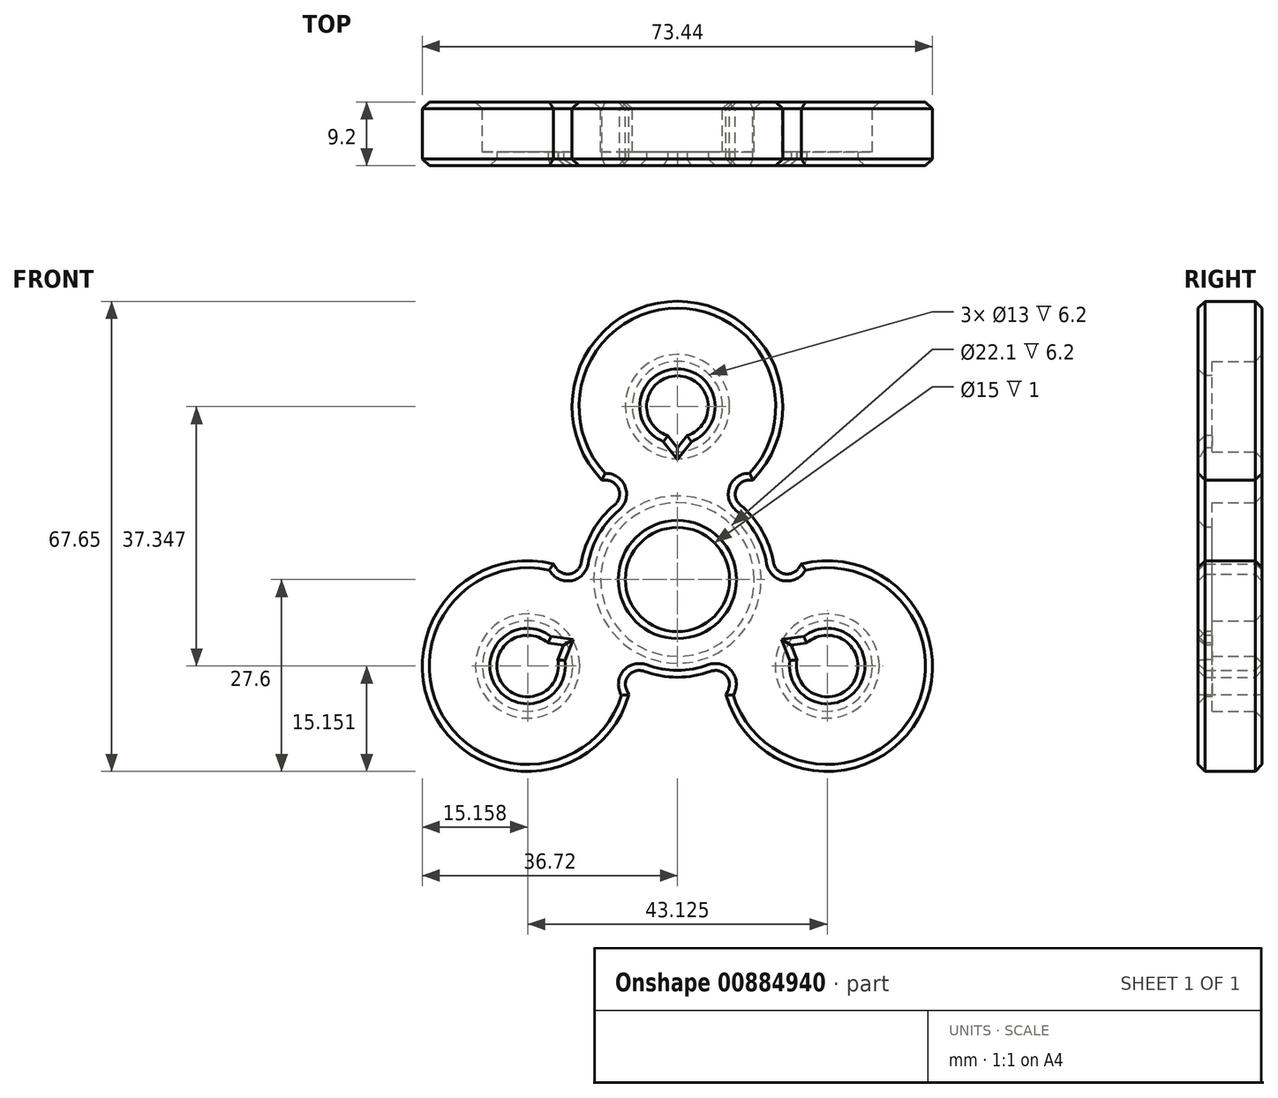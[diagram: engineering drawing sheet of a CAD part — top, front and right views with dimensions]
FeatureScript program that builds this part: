
annotation { "Feature Type Name" : "Feature", "Feature Type Description" : "" }
export const myFeature = defineFeature(function(context is Context, id is Id, definition is map)
    precondition{}
    {
        {
            var Q0;
            Q0=qCreatedBy(makeId("Front.planeOp"),FACE);
            var sketch = newSketch(context, id + "F0", { "sketchPlane" : qUnion([Q0])});
            skCircle(sketch, "E0", {"center": v(0, 0) * mm, "radius": 11.05 * mm});
            skArc(sketch, "E1", {"start": v(-2.48, 13.83) * mm, "mid": v(-12.17, 7.02) * mm, "end": v(-13.22, -4.76) * mm});
            skArc(sketch, "E2.MirrorC", {"start": v(-10.86, 14.33) * mm, "mid": v(0, 40.05) * mm, "end": v(10.86, 14.33) * mm});
            skArc(sketch, "E3.1.0", {"start": v(-6.98, -16.57) * mm, "mid": v(-34.69, -20.03) * mm, "end": v(-17.84, 2.24) * mm});
            skArc(sketch, "E3.2.0", {"start": v(17.84, 2.24) * mm, "mid": v(34.69, -20.03) * mm, "end": v(6.98, -16.57) * mm});
            skLineSegment(sketch, "E4", {"start": v(-10.86, 14.33) * mm, "end": v(-2.48, 13.83) * mm});
            skLineSegment(sketch, "E5.MirrorCS", {"start": v(10.86, 14.33) * mm, "end": v(2.48, 13.83) * mm});
            skLineSegment(sketch, "E6.1.0", {"start": v(-6.98, -16.57) * mm, "end": v(-10.73, -9.06) * mm});
            skLineSegment(sketch, "E6.1.1", {"start": v(-17.84, 2.24) * mm, "end": v(-13.22, -4.76) * mm});
            skLineSegment(sketch, "E6.2.0", {"start": v(17.84, 2.24) * mm, "end": v(13.22, -4.76) * mm});
            skLineSegment(sketch, "E6.2.1", {"start": v(6.98, -16.57) * mm, "end": v(10.73, -9.06) * mm});
            skArc(sketch, "E7.trimOffspring", {"start": v(13.22, -4.76) * mm, "mid": v(12.17, 7.03) * mm, "end": v(2.48, 13.83) * mm});
            skArc(sketch, "E8.trimOffspring", {"start": v(-10.73, -9.06) * mm, "mid": v(0, -14.05) * mm, "end": v(10.73, -9.06) * mm});
            skCircle(sketch, "E9", {"center": v(-21.56, -12.45) * mm, "radius": 6.5 * mm});
            skCircle(sketch, "E10.1.0", {"center": v(21.56, -12.45) * mm, "radius": 6.5 * mm});
            skCircle(sketch, "E10.2.0", {"center": v(0, 24.9) * mm, "radius": 6.5 * mm});
            skSolve(sketch);
        }
        {
            var Q0;
            Q0=qSketchRegion(id+"F0",true);
            extrude(context, id + "F1", {"entities" : qUnion([Q0]), "depth" : 9.2 * mm, "offsetDistance" : 25 * mm});
        }
        {
            var Q0;
            Q0=makeQuery(id+"F1.opExtrude","CAP_FACE",FACE,{"disambiguationData":[OSD([sQuery(id+"F0.wireOp",EDGE,"E0"),sQuery(id+"F0.wireOp",EDGE,"E1"),sQuery(id+"F0.wireOp",EDGE,"270d9bb9-0240-4263-a567-a3f57c0ecbf70.MirrorC"),sQuery(id+"F0.wireOp",EDGE,"E2.MirrorC"),sQuery(id+"F0.wireOp",EDGE,"E3.1.0"),sQuery(id+"F0.wireOp",EDGE,"E3.1.1"),sQuery(id+"F0.wireOp",EDGE,"E3.2.0"),sQuery(id+"F0.wireOp",EDGE,"E3.2.1"),sQuery(id+"F0.wireOp",EDGE,"E4"),sQuery(id+"F0.wireOp",EDGE,"E5.MirrorCS"),sQuery(id+"F0.wireOp",EDGE,"E6.1.0"),sQuery(id+"F0.wireOp",EDGE,"E6.1.1"),sQuery(id+"F0.wireOp",EDGE,"E6.2.0"),sQuery(id+"F0.wireOp",EDGE,"E6.2.1"),sQuery(id+"F0.wireOp",EDGE,"E7.trimOffspring"),sQuery(id+"F0.wireOp",EDGE,"E8.trimOffspring")])],"isStart":false});
            var sketch = newSketch(context, id + "F2", { "sketchPlane" : qUnion([Q0])});
            skCircle(sketch, "E11", {"center": v(0, 24.9) * mm, "radius": 4.43 * mm});
            skCircle(sketch, "E12.1.0", {"center": v(-21.56, -12.45) * mm, "radius": 4.43 * mm});
            skCircle(sketch, "E12.2.0", {"center": v(21.56, -12.45) * mm, "radius": 4.43 * mm});
            skPoint(sketch, "E12.center", {"position": v(0, 0) * mm});
            skCircle(sketch, "E13", {"center": v(0, 24.9) * mm, "radius": 7.5 * mm});
            skCircle(sketch, "E14.1.0", {"center": v(-21.56, -12.45) * mm, "radius": 7.5 * mm});
            skCircle(sketch, "E14.2.0", {"center": v(21.56, -12.45) * mm, "radius": 7.5 * mm});
            skCircle(sketch, "E15", {"center": v(0, 0) * mm, "radius": 11.05 * mm});
            skCircle(sketch, "E16", {"center": v(0, 0) * mm, "radius": 7.5 * mm});
            skSolve(sketch);
        }
        {
            var Q0;
            Q0=qSketchRegion(id+"F2",true);
            extrude(context, id + "F3", {"entities" : qUnion([Q0]), "operationType" : NewBodyOperationType.ADD, "oppositeDirection" : true, "depth" : 2 * mm, "offsetDistance" : 25 * mm});
        }
        {
            var Q0;
            Q0=makeQuery(id+"F1.opExtrude","SWEPT_EDGE",EDGE,{"disambiguationData":[OSD([sQuery(id+"F0.wireOp",EDGE,"E5.MirrorCS"),sQuery(id+"F0.wireOp",EDGE,"E7.trimOffspring")])]});
            var Q1;
            Q1=makeQuery(id+"F1.opExtrude","SWEPT_EDGE",EDGE,{"disambiguationData":[OSD([sQuery(id+"F0.wireOp",EDGE,"E1"),sQuery(id+"F0.wireOp",EDGE,"E4")])]});
            var Q2;
            Q2=makeQuery(id+"F1.opExtrude","SWEPT_EDGE",EDGE,{"disambiguationData":[OSD([sQuery(id+"F0.wireOp",EDGE,"E1"),sQuery(id+"F0.wireOp",EDGE,"E6.1.1")])]});
            var Q3;
            Q3=makeQuery(id+"F1.opExtrude","SWEPT_EDGE",EDGE,{"disambiguationData":[OSD([sQuery(id+"F0.wireOp",EDGE,"E6.1.0"),sQuery(id+"F0.wireOp",EDGE,"E8.trimOffspring")])]});
            var Q4;
            Q4=makeQuery(id+"F1.opExtrude","SWEPT_EDGE",EDGE,{"disambiguationData":[OSD([sQuery(id+"F0.wireOp",EDGE,"E6.2.1"),sQuery(id+"F0.wireOp",EDGE,"E8.trimOffspring")])]});
            var Q5;
            Q5=makeQuery(id+"F1.opExtrude","SWEPT_EDGE",EDGE,{"disambiguationData":[OSD([sQuery(id+"F0.wireOp",EDGE,"E6.2.0"),sQuery(id+"F0.wireOp",EDGE,"E7.trimOffspring")])]});
            fillet(context, id + "F4", {"entities" : qUnion([Q0, Q1, Q2, Q3, Q4, Q5]), "radius" : 2 * mm, "tangentPropagation" : true, "allowEdgeOverflow" : false});
        }
        {
            var Q0;
            Q0=makeQuery(id+"F1.opExtrude","CAP_FACE",FACE,{"disambiguationData":[OSD([sQuery(id+"F0.wireOp",EDGE,"E0"),sQuery(id+"F0.wireOp",EDGE,"E1"),sQuery(id+"F0.wireOp",EDGE,"270d9bb9-0240-4263-a567-a3f57c0ecbf70.MirrorC"),sQuery(id+"F0.wireOp",EDGE,"E2.MirrorC"),sQuery(id+"F0.wireOp",EDGE,"E3.1.0"),sQuery(id+"F0.wireOp",EDGE,"E3.1.1"),sQuery(id+"F0.wireOp",EDGE,"E3.2.0"),sQuery(id+"F0.wireOp",EDGE,"E3.2.1"),sQuery(id+"F0.wireOp",EDGE,"E4"),sQuery(id+"F0.wireOp",EDGE,"E5.MirrorCS"),sQuery(id+"F0.wireOp",EDGE,"E6.1.0"),sQuery(id+"F0.wireOp",EDGE,"E6.1.1"),sQuery(id+"F0.wireOp",EDGE,"E6.2.0"),sQuery(id+"F0.wireOp",EDGE,"E6.2.1"),sQuery(id+"F0.wireOp",EDGE,"E7.trimOffspring"),sQuery(id+"F0.wireOp",EDGE,"E8.trimOffspring")])],"isStart":false});
            var sketch = newSketch(context, id + "F5", { "sketchPlane" : qUnion([Q0])});
            skArc(sketch, "E17", {"start": v(1.77, 21.17) * mm, "mid": v(0, 24.92) * mm, "end": v(-1.77, 21.17) * mm});
            skLineSegment(sketch, "E18", {"start": v(-1.77, 21.17) * mm, "end": v(0, 18.91) * mm});
            skLineSegment(sketch, "E19", {"start": v(1.77, 21.17) * mm, "end": v(0, 18.91) * mm});
            skPoint(sketch, "E20.orphan", {"position": v(1.84, 21.27) * mm});
            skPoint(sketch, "E21.orphan", {"position": v(-1.84, 21.27) * mm});
            skArc(sketch, "E22.1.0", {"start": v(-19.22, -9.06) * mm, "mid": v(-21.58, -12.46) * mm, "end": v(-17.45, -12.12) * mm});
            skLineSegment(sketch, "E22.1.1", {"start": v(-17.45, -12.12) * mm, "end": v(-16.38, -9.46) * mm});
            skLineSegment(sketch, "E22.1.2", {"start": v(-19.22, -9.06) * mm, "end": v(-16.38, -9.46) * mm});
            skArc(sketch, "E22.2.0", {"start": v(17.45, -12.12) * mm, "mid": v(21.58, -12.46) * mm, "end": v(19.22, -9.06) * mm});
            skLineSegment(sketch, "E22.2.1", {"start": v(19.22, -9.06) * mm, "end": v(16.38, -9.46) * mm});
            skLineSegment(sketch, "E22.2.2", {"start": v(17.45, -12.12) * mm, "end": v(16.38, -9.46) * mm});
            skPoint(sketch, "E22.center", {"position": v(0, 0) * mm});
            skSolve(sketch);
        }
        {
            var Q0;
            Q0=qSketchRegion(id+"F5",true);
            extrude(context, id + "F6", {"entities" : qUnion([Q0]), "operationType" : NewBodyOperationType.REMOVE, "oppositeDirection" : true, "depth" : 25 * mm, "offsetDistance" : 25 * mm});
        }
        {
            var Q0;
            Q0=makeQuery(id+"F1.opExtrude","CAP_FACE",FACE,{"disambiguationData":[OSD([sQuery(id+"F0.wireOp",EDGE,"E0"),sQuery(id+"F0.wireOp",EDGE,"E1"),sQuery(id+"F0.wireOp",EDGE,"270d9bb9-0240-4263-a567-a3f57c0ecbf70.MirrorC"),sQuery(id+"F0.wireOp",EDGE,"E2.MirrorC"),sQuery(id+"F0.wireOp",EDGE,"E3.1.0"),sQuery(id+"F0.wireOp",EDGE,"E3.1.1"),sQuery(id+"F0.wireOp",EDGE,"E3.2.0"),sQuery(id+"F0.wireOp",EDGE,"E3.2.1"),sQuery(id+"F0.wireOp",EDGE,"E4"),sQuery(id+"F0.wireOp",EDGE,"E5.MirrorCS"),sQuery(id+"F0.wireOp",EDGE,"E6.1.0"),sQuery(id+"F0.wireOp",EDGE,"E6.1.1"),sQuery(id+"F0.wireOp",EDGE,"E6.2.0"),sQuery(id+"F0.wireOp",EDGE,"E6.2.1"),sQuery(id+"F0.wireOp",EDGE,"E7.trimOffspring"),sQuery(id+"F0.wireOp",EDGE,"E8.trimOffspring")])],"isStart":true});
            chamfer(context, id + "F7", {"entities" : qUnion([Q0]), "width" : 1 * mm, "tangentPropagation" : true});
        }
        {
            var Q0;
            Q0=makeQuery(id+"F3.boolean.opBoolean","MERGE",FACE,{"derivedFrom":[makeQuery(id+"F1.opExtrude","CAP_FACE",FACE,{"disambiguationData":[OSD([sQuery(id+"F0.wireOp",EDGE,"E0"),sQuery(id+"F0.wireOp",EDGE,"E1"),sQuery(id+"F0.wireOp",EDGE,"270d9bb9-0240-4263-a567-a3f57c0ecbf70.MirrorC"),sQuery(id+"F0.wireOp",EDGE,"E2.MirrorC"),sQuery(id+"F0.wireOp",EDGE,"E3.1.0"),sQuery(id+"F0.wireOp",EDGE,"E3.1.1"),sQuery(id+"F0.wireOp",EDGE,"E3.2.0"),sQuery(id+"F0.wireOp",EDGE,"E3.2.1"),sQuery(id+"F0.wireOp",EDGE,"E4"),sQuery(id+"F0.wireOp",EDGE,"E5.MirrorCS"),sQuery(id+"F0.wireOp",EDGE,"E6.1.0"),sQuery(id+"F0.wireOp",EDGE,"E6.1.1"),sQuery(id+"F0.wireOp",EDGE,"E6.2.0"),sQuery(id+"F0.wireOp",EDGE,"E6.2.1"),sQuery(id+"F0.wireOp",EDGE,"E7.trimOffspring"),sQuery(id+"F0.wireOp",EDGE,"E8.trimOffspring")])],"isStart":false}),makeQuery(id+"F3.opExtrude","CAP_FACE",FACE,{"disambiguationData":[OSD([sQuery(id+"F2.wireOp",EDGE,"E11"),sQuery(id+"F2.wireOp",EDGE,"E13")])],"isStart":true}),makeQuery(id+"F3.opExtrude","CAP_FACE",FACE,{"disambiguationData":[OSD([sQuery(id+"F2.wireOp",EDGE,"E12.1.0"),sQuery(id+"F2.wireOp",EDGE,"E14.1.0")])],"isStart":true}),makeQuery(id+"F3.opExtrude","CAP_FACE",FACE,{"disambiguationData":[OSD([sQuery(id+"F2.wireOp",EDGE,"E12.2.0"),sQuery(id+"F2.wireOp",EDGE,"E14.2.0")])],"isStart":true}),makeQuery(id+"F3.opExtrude","CAP_FACE",FACE,{"disambiguationData":[OSD([sQuery(id+"F2.wireOp",EDGE,"E15"),sQuery(id+"F2.wireOp",EDGE,"E16")])],"isStart":true})]});
            chamfer(context, id + "F8", {"entities" : qUnion([Q0]), "width" : 1 * mm, "tangentPropagation" : true});
        }
    });
